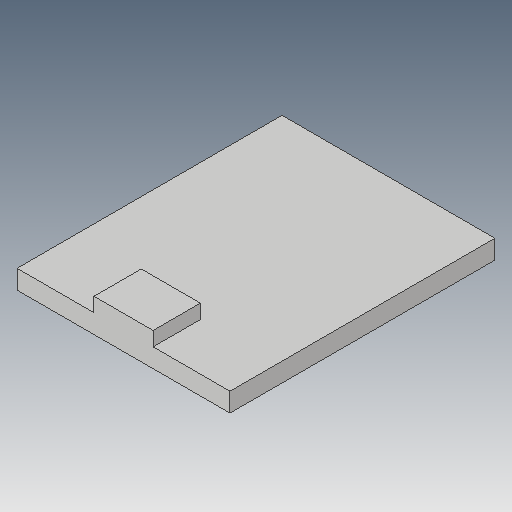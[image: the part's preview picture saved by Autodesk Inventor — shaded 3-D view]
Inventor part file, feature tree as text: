
AUTODESK INVENTOR PART (.ipt)
format: ipt  version: 2018 (Build 220112000, 112)  size: 93,184 bytes
history: native  units: mm
features: extrude x2, sketch x2
ambient origin geometry x8: Origin, YZ Plane, XZ Plane, XY Plane, X Axis, Y Axis, Z Axis, Center Point
bodies: Solid1 (feature_tree)
feature tree (4):
  extrude  "Extrusion1"  Depth=45.0mm
  extrude  "Extrusion2"  Depth=12.5mm
  sketch  "Sketch1"  dims[d0=56.0mm d1=45.0mm]
  sketch  "Sketch2"  dims[d2=4.0mm d3=0.0mm d4=12.5mm d5=10.0mm d6=3.0mm d7=0.0mm]
